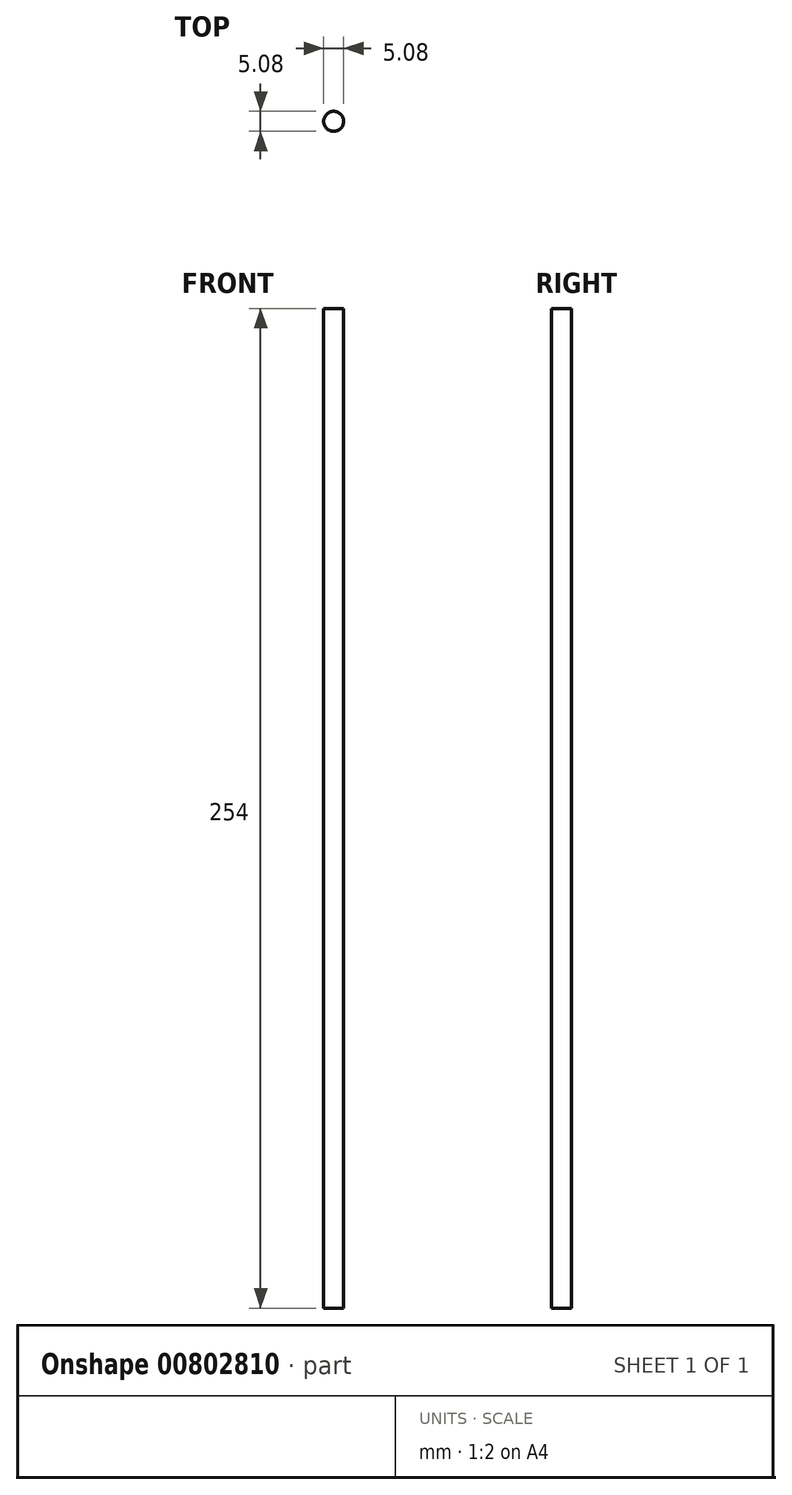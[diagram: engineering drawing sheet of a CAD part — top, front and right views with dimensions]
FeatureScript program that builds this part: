
annotation { "Feature Type Name" : "Feature", "Feature Type Description" : "" }
export const myFeature = defineFeature(function(context is Context, id is Id, definition is map)
    precondition{}
    {
        {
            var Q0;
            Q0=qCreatedBy(makeId("Top.planeOp"),FACE);
            var sketch = newSketch(context, id + "F0", { "sketchPlane" : qUnion([Q0])});
            skCircle(sketch, "E0", {"center": v(0, 0) * mm, "radius": 2.54 * mm});
            skSolve(sketch);
        }
        {
            var Q0;
            Q0=makeQuery(id+"F0.imprint","IMPRINT",FACE,{"disambiguationData":[TD([[makeQuery(id+"F0.imprint","IMPRINT",EDGE,{"derivedFrom":sQuery(id+"F0.wireOp",EDGE,"E0")}),1.0]])]});
            extrude(context, id + "F1", {"entities" : qUnion([Q0]), "depth" : 254 * mm, "offsetDistance" : 25.4 * mm});
        }
    });
